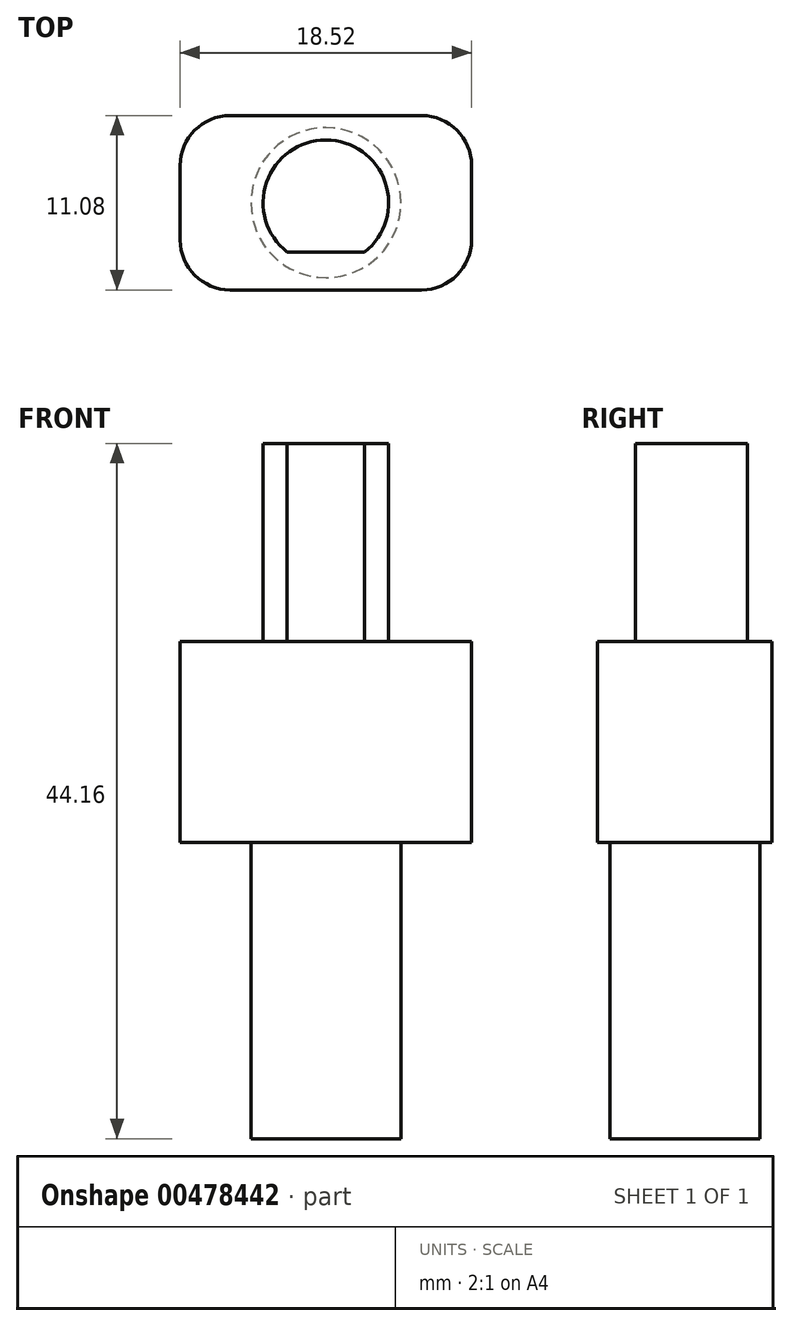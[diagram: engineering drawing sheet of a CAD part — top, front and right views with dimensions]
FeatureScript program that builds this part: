
annotation { "Feature Type Name" : "Feature", "Feature Type Description" : "" }
export const myFeature = defineFeature(function(context is Context, id is Id, definition is map)
    precondition{}
    {
        {
            var Q0;
            Q0=qCreatedBy(makeId("Top.planeOp"),FACE);
            var sketch = newSketch(context, id + "F0", { "sketchPlane" : qUnion([Q0])});
            skCircle(sketch, "E0", {"center": v(0, 0) * mm, "radius": 4.76 * mm});
            skSolve(sketch);
        }
        {
            var Q0;
            Q0 = qSketchRegion(id + "F0", true);
            extrude(context, id + "F1", {"entities" : qUnion([Q0]), "depth" : 18.8 * mm, "offsetDistance" : 25.4 * mm});
        }
        {
            var Q0;
            Q0=makeQuery(id+"F1.opExtrude","CAP_FACE",FACE,{"disambiguationData":[OSD([sQuery(id+"F0.wireOp",EDGE,"E0")])],"isStart":false});
            var sketch = newSketch(context, id + "F2", { "sketchPlane" : qUnion([Q0])});
            skLineSegment(sketch, "E1.bottom", {"start": v(6.08, 5.54) * mm, "end": v(-6.08, 5.54) * mm});
            skLineSegment(sketch, "E1.top", {"start": v(6.08, -5.54) * mm, "end": v(-6.08, -5.54) * mm});
            skLineSegment(sketch, "E1.left", {"start": v(9.26, 2.36) * mm, "end": v(9.26, -2.36) * mm});
            skLineSegment(sketch, "E1.right", {"start": v(-9.26, 2.36) * mm, "end": v(-9.26, -2.36) * mm});
            skPoint(sketch, "E1.middle", {"position": v(0, 0) * mm});
            skPoint(sketch, "E2.visualSharp", {"position": v(-9.26, 5.54) * mm});
            skArc(sketch, "E2.filletArc", {"start": v(-6.08, 5.54) * mm, "mid": v(-8.33, 4.6) * mm, "end": v(-9.26, 2.36) * mm});
            skPoint(sketch, "E3.visualSharp", {"position": v(-9.26, -5.54) * mm});
            skArc(sketch, "E3.filletArc", {"start": v(-9.26, -2.36) * mm, "mid": v(-8.33, -4.6) * mm, "end": v(-6.08, -5.54) * mm});
            skPoint(sketch, "E4.visualSharp", {"position": v(9.26, -5.54) * mm});
            skArc(sketch, "E4.filletArc", {"start": v(6.08, -5.54) * mm, "mid": v(8.33, -4.6) * mm, "end": v(9.26, -2.36) * mm});
            skPoint(sketch, "E5.visualSharp", {"position": v(9.26, 5.54) * mm});
            skArc(sketch, "E5.filletArc", {"start": v(9.26, 2.36) * mm, "mid": v(8.33, 4.6) * mm, "end": v(6.08, 5.54) * mm});
            skSolve(sketch);
        }
        {
            var Q0;
            Q0 = qSketchRegion(id + "F2", true);
            extrude(context, id + "F3", {"entities" : qUnion([Q0]), "operationType" : NewBodyOperationType.ADD, "depth" : 12.78 * mm, "offsetDistance" : 25.4 * mm});
        }
        {
            var Q0;
            Q0=makeQuery(id+"F3.opExtrude","CAP_FACE",FACE,{"disambiguationData":[OSD([sQuery(id+"F2.wireOp",EDGE,"E1.bottom"),sQuery(id+"F2.wireOp",EDGE,"E1.top"),sQuery(id+"F2.wireOp",EDGE,"E1.left"),sQuery(id+"F2.wireOp",EDGE,"E1.right"),sQuery(id+"F2.wireOp",EDGE,"E2.filletArc"),sQuery(id+"F2.wireOp",EDGE,"E3.filletArc"),sQuery(id+"F2.wireOp",EDGE,"E4.filletArc"),sQuery(id+"F2.wireOp",EDGE,"E5.filletArc")])],"isStart":false});
            var sketch = newSketch(context, id + "F4", { "sketchPlane" : qUnion([Q0])});
            skCircle(sketch, "E6", {"center": v(0, 0) * mm, "radius": 3.99 * mm});
            skSolve(sketch);
        }
        {
            var Q0;
            Q0=makeQuery(id+"F4.imprint","IMPRINT",FACE,{"disambiguationData":[TD([[makeQuery(id+"F4.imprint","IMPRINT",EDGE,{"derivedFrom":sQuery(id+"F4.wireOp",EDGE,"E6")}),1.0]])]});
            extrude(context, id + "F5", {"entities" : qUnion([Q0]), "operationType" : NewBodyOperationType.ADD, "depth" : 12.57 * mm, "offsetDistance" : 25.4 * mm});
        }
        {
            var Q0;
            Q0=makeQuery(id+"F5.opExtrude","CAP_FACE",FACE,{"disambiguationData":[OSD([sQuery(id+"F4.wireOp",EDGE,"E6")])],"isStart":false});
            var sketch = newSketch(context, id + "F6", { "sketchPlane" : qUnion([Q0])});
            skLineSegment(sketch, "E7", {"start": v(0.48, -3.14) * mm, "end": v(2.46, -3.14) * mm});
            skLineSegment(sketch, "E8", {"start": v(2.46, -3.14) * mm, "end": v(-2.46, -3.14) * mm});
            skArc(sketch, "E9", {"start": v(-2.46, -3.14) * mm, "mid": v(0, -3.99) * mm, "end": v(2.46, -3.14) * mm});
            skSolve(sketch);
        }
        {
            var Q0;
            Q0 = qSketchRegion(id + "F6", true);
            extrude(context, id + "F7", {"entities" : qUnion([Q0]), "operationType" : NewBodyOperationType.REMOVE, "oppositeDirection" : true, "depth" : 12.57 * mm, "offsetDistance" : 25.4 * mm});
        }
    });
